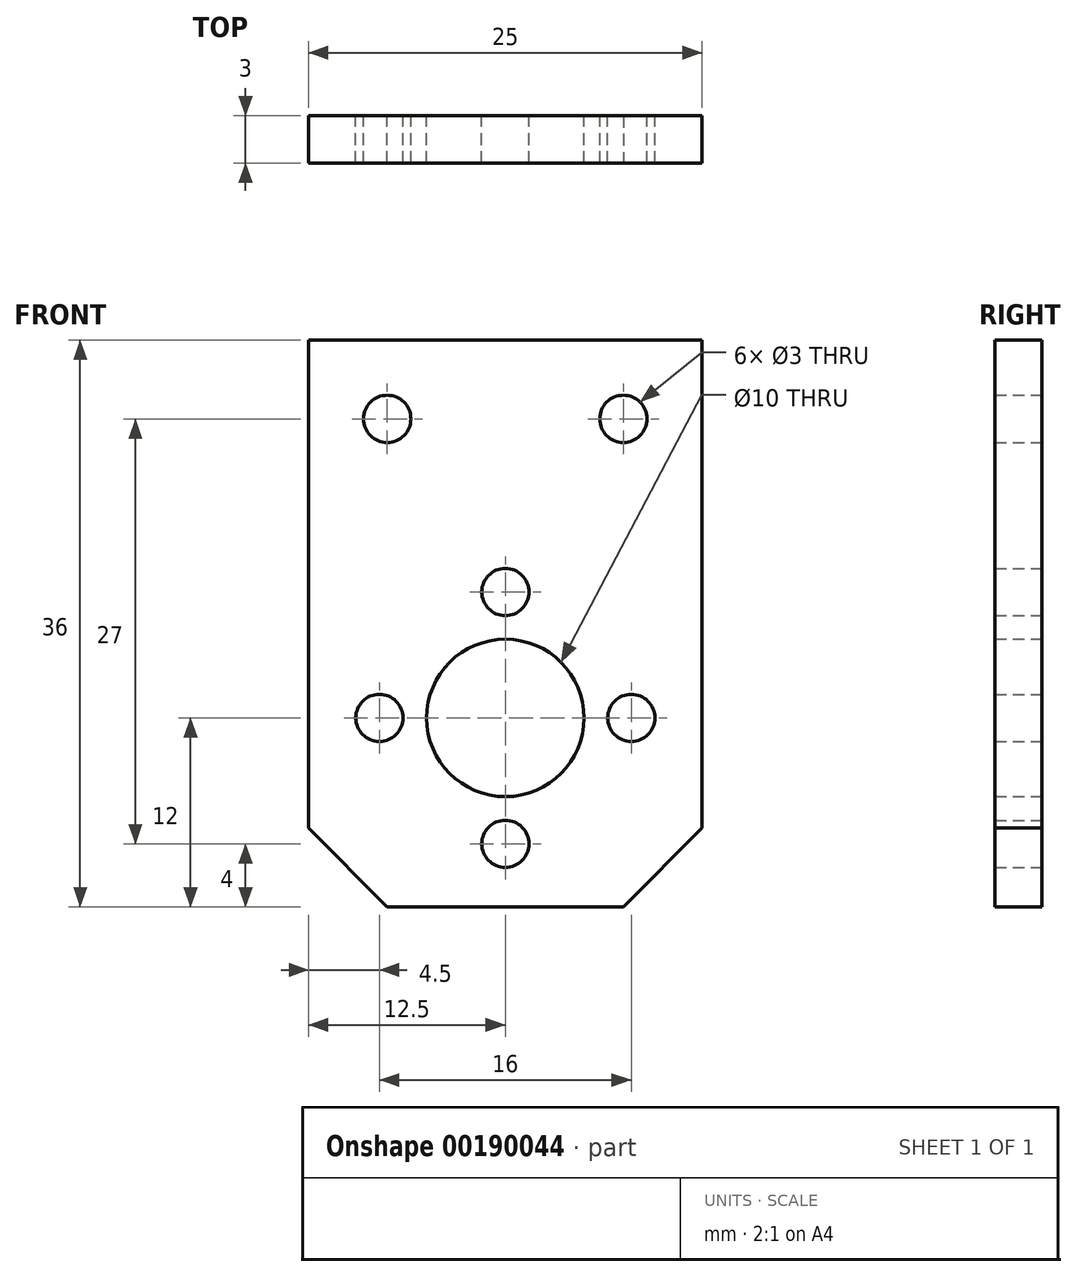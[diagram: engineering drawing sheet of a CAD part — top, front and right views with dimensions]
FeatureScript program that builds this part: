
annotation { "Feature Type Name" : "Feature", "Feature Type Description" : "" }
export const myFeature = defineFeature(function(context is Context, id is Id, definition is map)
    precondition{}
    {
        {
            var Q0;
            Q0=qCreatedBy(makeId("Front.planeOp"),FACE);
            var sketch = newSketch(context, id + "F0", { "sketchPlane" : qUnion([Q0])});
            skLineSegment(sketch, "E0.top", {"start": v(-12.5, 24) * mm, "end": v(12.5, 24) * mm});
            skLineSegment(sketch, "E0.left", {"start": v(-12.5, -12) * mm, "end": v(-12.5, 24) * mm});
            skLineSegment(sketch, "E0.right", {"start": v(12.5, -12) * mm, "end": v(12.5, 24) * mm});
            skPoint(sketch, "E0.middle", {"position": v(0, 0) * mm});
            skCircle(sketch, "E1", {"center": v(0, 0) * mm, "radius": 5 * mm});
            skCircle(sketch, "E2", {"center": v(0, 8) * mm, "radius": 1.5 * mm});
            skCircle(sketch, "E3.1.0", {"center": v(-8, 0) * mm, "radius": 1.5 * mm});
            skCircle(sketch, "E3.2.0", {"center": v(0, -8) * mm, "radius": 1.5 * mm});
            skCircle(sketch, "E3.3.0", {"center": v(8, 0) * mm, "radius": 1.5 * mm});
            skCircle(sketch, "E4", {"center": v(-7.5, 19) * mm, "radius": 1.5 * mm});
            skLineSegment(sketch, "E5", {"start": v(-12.5, 0) * mm, "end": v(12.5, 0) * mm, "construction": true});
            skCircle(sketch, "E6", {"center": v(0, 0) * mm, "radius": 11 * mm, "construction": true});
            skLineSegment(sketch, "E7", {"start": v(-12.5, -12) * mm, "end": v(12.5, -12) * mm});
            skLineSegment(sketch, "E8", {"start": v(0, 24) * mm, "end": v(0, -12) * mm, "construction": true});
            skCircle(sketch, "E9.MirrorC", {"center": v(7.5, 19) * mm, "radius": 1.5 * mm});
            skSolve(sketch);
        }
        {
            var Q0;
            Q0=qSketchRegion(id+"F0",true);
            extrude(context, id + "F1", {"entities" : qUnion([Q0]), "depth" : 3 * mm});
        }
        {
            var Q0;
            Q0=makeQuery(id+"F1.opExtrude","SWEPT_EDGE",EDGE,{"disambiguationData":[OSD([sQuery(id+"F0.wireOp",EDGE,"E0.left"),sQuery(id+"F0.wireOp",EDGE,"E7")])]});
            var Q1;
            Q1=makeQuery(id+"F1.opExtrude","SWEPT_EDGE",EDGE,{"disambiguationData":[OSD([sQuery(id+"F0.wireOp",EDGE,"E0.right"),sQuery(id+"F0.wireOp",EDGE,"E7")])]});
            chamfer(context, id + "F2", {"entities" : qUnion([Q0, Q1]), "width" : 5 * mm, "tangentPropagation" : true});
        }
    });
